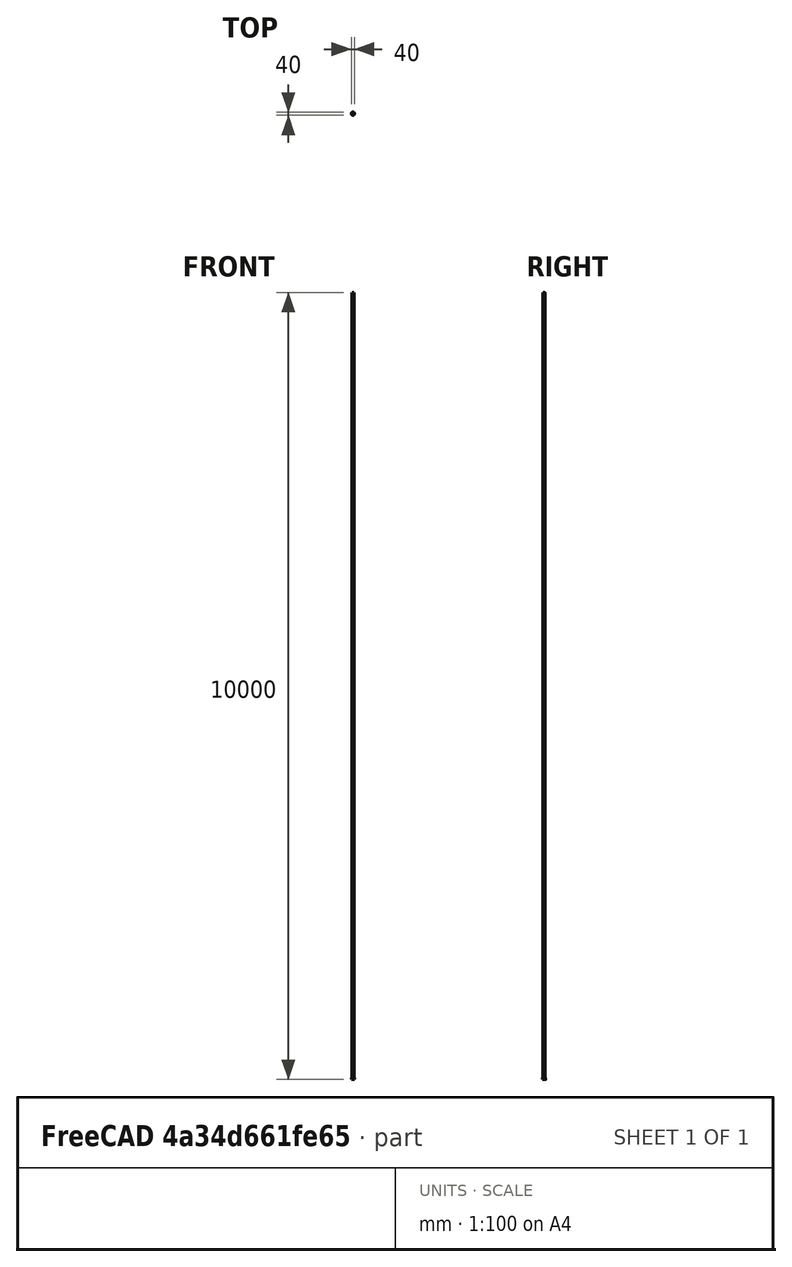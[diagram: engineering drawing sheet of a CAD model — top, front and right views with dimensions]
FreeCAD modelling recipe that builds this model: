
FCSTD DOCUMENT  (FreeCAD 0.16R)
Label: broachpullerbush3
License: All rights reserved
LicenseURL: http://en.wikipedia.org/wiki/All_rights_reserved
objects: Sketcher::SketchObject×3, PartDesign::Pocket×2, PartDesign::Pad×1, Mesh::Feature×1
note: 9 computed .brp shape members not serialized (recipe doc carries the construction recipe); baked Part::Feature solids carry a one-line shape summary decoded from their .brp

FEATURE [Sketcher::SketchObject] Sketch
  sketch-geometry (1):
    g0: Circle CenterX=0 CenterY=0 CenterZ=0 NormalX=0 NormalY=0 NormalZ=1 Radius=20
  constraints (2):
    c: Coincident(g0,g-1)
    c: Radius(g0) = 20
FEATURE [PartDesign::Pad] Pad
  Length = 20
  Length2 = 100
  Sketch = -> Sketch
  Type = 0
FEATURE [Sketcher::SketchObject] Sketch001
  Placement = pos=(0,0,20) rot=(0,0,1;0rad)
  Support = -> Pad [Face3]
  sketch-geometry (1):
    g0: Circle CenterX=0 CenterY=0 CenterZ=0 NormalX=0 NormalY=0 NormalZ=1 Radius=15.25
  constraints (2):
    c: Coincident(g0,g-1)
    c: Radius(g0) = 15.25
FEATURE [PartDesign::Pocket] Pocket
  Length = 10
  Sketch = -> Sketch001
  Type = 0
FEATURE [Sketcher::SketchObject] Sketch002
  Placement = pos=(0,0,0) rot=(1,0,0;3.14159rad)
  Support = -> Pocket [Face2]
  sketch-geometry (1):
    g0: Circle CenterX=0 CenterY=0 CenterZ=0 NormalX=0 NormalY=0 NormalZ=1 Radius=12.65
  constraints (2):
    c: Coincident(g0,g-1)
    c: Radius(g0) = 12.65
FEATURE [PartDesign::Pocket] Pocket001
  Length = 5
  Sketch = -> Sketch002
  Type = 1
FEATURE [Mesh::Feature] Mesh  label="Pocket001 (Meshed)"
